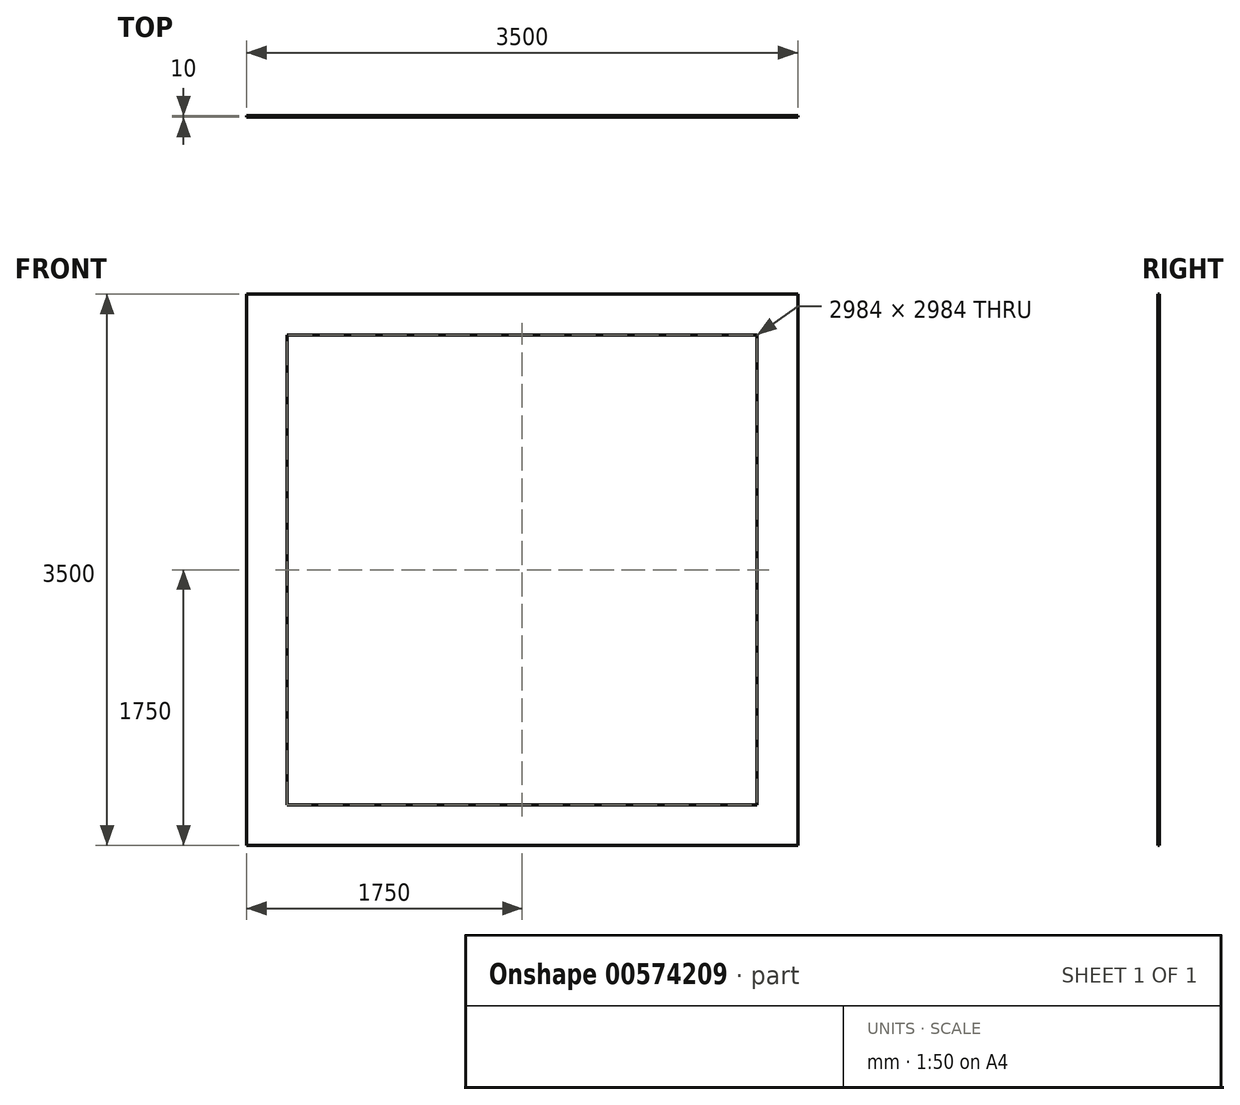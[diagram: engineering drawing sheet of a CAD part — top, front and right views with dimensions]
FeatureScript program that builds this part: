
annotation { "Feature Type Name" : "Feature", "Feature Type Description" : "" }
export const myFeature = defineFeature(function(context is Context, id is Id, definition is map)
    precondition{}
    {
        {
            var Q0;
            Q0=qCreatedBy(makeId("Front.planeOp"),FACE);
            var sketch = newSketch(context, id + "F0", { "sketchPlane" : qUnion([Q0])});
            skLineSegment(sketch, "E0.bottom", {"start": v(0, 0) * mm, "end": v(3500, 0) * mm});
            skLineSegment(sketch, "E0.top", {"start": v(0, 3500) * mm, "end": v(3500, 3500) * mm});
            skLineSegment(sketch, "E0.left", {"start": v(0, 0) * mm, "end": v(0, 3500) * mm});
            skLineSegment(sketch, "E0.right", {"start": v(3500, 0) * mm, "end": v(3500, 3500) * mm});
            skLineSegment(sketch, "E1.0", {"start": v(258, 3242) * mm, "end": v(3242, 3242) * mm});
            skLineSegment(sketch, "E1.1", {"start": v(258, 258) * mm, "end": v(258, 3242) * mm});
            skLineSegment(sketch, "E1.2", {"start": v(258, 258) * mm, "end": v(3242, 258) * mm});
            skLineSegment(sketch, "E1.3", {"start": v(3242, 258) * mm, "end": v(3242, 3242) * mm});
            skSolve(sketch);
        }
        {
            var Q0;
            Q0=makeQuery(id+"F0.imprint","IMPRINT",FACE,{"disambiguationData":[TD([[makeQuery(id+"F0.imprint","IMPRINT",EDGE,{"derivedFrom":sQuery(id+"F0.wireOp",EDGE,"E0.bottom")}),1.0]])]});
            extrude(context, id + "F1", {"entities" : qUnion([Q0]), "depth" : 10 * mm, "offsetDistance" : 25 * mm});
        }
    });
